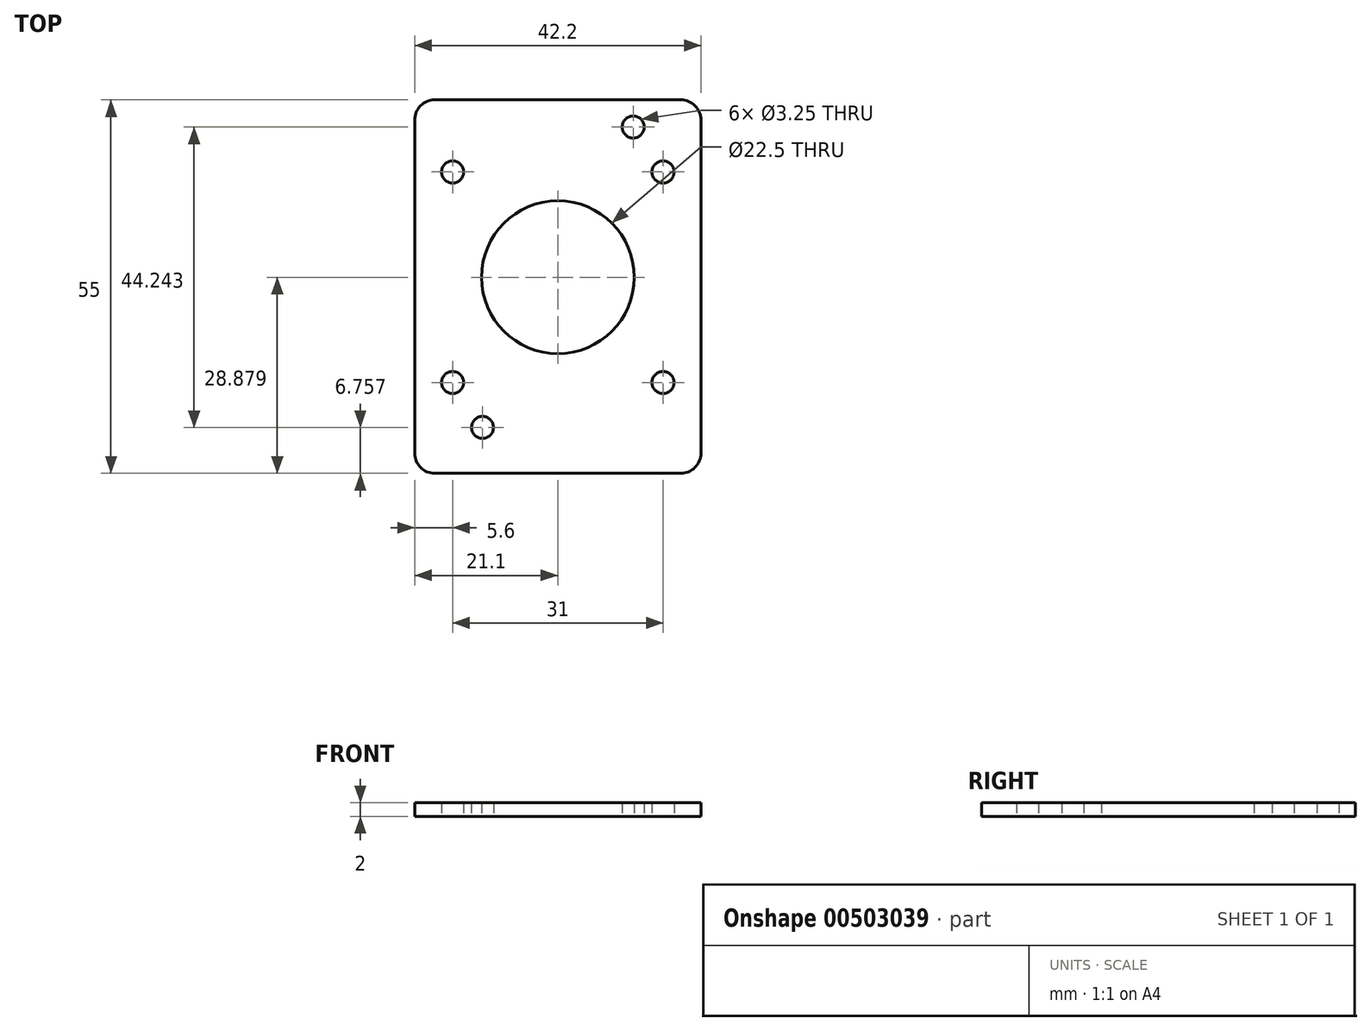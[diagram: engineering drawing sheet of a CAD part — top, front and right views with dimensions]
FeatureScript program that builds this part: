
annotation { "Feature Type Name" : "Feature", "Feature Type Description" : "" }
export const myFeature = defineFeature(function(context is Context, id is Id, definition is map)
    precondition{}
    {
        {
            var Q0;
            Q0=qCreatedBy(makeId("Top.planeOp"),FACE);
            var sketch = newSketch(context, id + "F0", { "sketchPlane" : qUnion([Q0])});
            skLineSegment(sketch, "E0.bottom", {"start": v(0, 0) * mm, "end": v(42.2, 0) * mm});
            skLineSegment(sketch, "E0.top", {"start": v(0, 55) * mm, "end": v(42.2, 55) * mm});
            skLineSegment(sketch, "E0.left", {"start": v(0, 0) * mm, "end": v(0, 55) * mm});
            skLineSegment(sketch, "E0.right", {"start": v(42.2, 0) * mm, "end": v(42.2, 55) * mm});
            skCircle(sketch, "E1", {"center": v(32.2, 51) * mm, "radius": 1.63 * mm});
            skLineSegment(sketch, "E2", {"start": v(32.2, 51) * mm, "end": v(10, 6.76) * mm});
            skCircle(sketch, "E3", {"center": v(21.1, 28.88) * mm, "radius": 11.25 * mm});
            skLineSegment(sketch, "E4", {"start": v(21.1, 55) * mm, "end": v(21.1, 0) * mm, "construction": true});
            skCircle(sketch, "E5", {"center": v(10, 6.76) * mm, "radius": 1.63 * mm});
            skLineSegment(sketch, "E6.bottom", {"start": v(5.6, 44.38) * mm, "end": v(36.6, 44.38) * mm});
            skLineSegment(sketch, "E6.top", {"start": v(5.6, 13.38) * mm, "end": v(36.6, 13.38) * mm});
            skLineSegment(sketch, "E6.left", {"start": v(5.6, 44.38) * mm, "end": v(5.6, 13.38) * mm});
            skLineSegment(sketch, "E6.right", {"start": v(36.6, 44.38) * mm, "end": v(36.6, 13.38) * mm});
            skCircle(sketch, "E7", {"center": v(5.6, 44.38) * mm, "radius": 1.63 * mm});
            skCircle(sketch, "E8", {"center": v(36.6, 44.38) * mm, "radius": 1.63 * mm});
            skCircle(sketch, "E9", {"center": v(36.6, 13.38) * mm, "radius": 1.63 * mm});
            skCircle(sketch, "E10", {"center": v(5.6, 13.38) * mm, "radius": 1.63 * mm});
            skSolve(sketch);
        }
        {
            var Q0;
            Q0=makeQuery(id+"F0.imprint","IMPRINT",FACE,{"disambiguationData":[TD([[makeQuery(id+"F0.imprint","IMPRINT",EDGE,{"derivedFrom":sQuery(id+"F0.wireOp",EDGE,"E0.bottom")}),1.0]])]});
            var Q1;
            {var subQ1=sQuery(id+"F0.wireOp",EDGE,"E2");var subQ4=sQuery(id+"F0.wireOp",EDGE,"E6.bottom");var subQ5=makeQuery(id+"F0.imprint","INTERSECT",VERTEX,{"derivedFrom":[subQ1,subQ4]});Q1=makeQuery(id+"F0.imprint","IMPRINT",FACE,{"disambiguationData":[TD([[makeQuery(id+"F0.imprint","IMPRINT",EDGE,{"disambiguationData":[TD([[subQ5,-1.0]])],"derivedFrom":subQ1}),-1.0]])]});}
            var Q2;
            {var subQ0=sQuery(id+"F0.wireOp",EDGE,"E6.bottom");var subQ1=sQuery(id+"F0.wireOp",EDGE,"E2");var subQ2=makeQuery(id+"F0.imprint","INTERSECT",VERTEX,{"derivedFrom":[subQ1,subQ0]});Q2=makeQuery(id+"F0.imprint","IMPRINT",FACE,{"disambiguationData":[TD([[makeQuery(id+"F0.imprint","IMPRINT",EDGE,{"disambiguationData":[TD([[subQ2,-1.0]])],"derivedFrom":subQ1}),1.0]])]});}
            extrude(context, id + "F1", {"entities" : qUnion([Q0, Q1, Q2]), "depth" : 2 * mm});
        }
        {
            var Q0;
            Q0=makeQuery(id+"F1.opExtrude","SWEPT_EDGE",EDGE,{"disambiguationData":[OSD([sQuery(id+"F0.wireOp",EDGE,"E0.top"),sQuery(id+"F0.wireOp",EDGE,"E0.right")])]});
            var Q1;
            Q1=makeQuery(id+"F1.opExtrude","SWEPT_EDGE",EDGE,{"disambiguationData":[OSD([sQuery(id+"F0.wireOp",EDGE,"E0.top"),sQuery(id+"F0.wireOp",EDGE,"E0.left")])]});
            var Q2;
            Q2=makeQuery(id+"F1.opExtrude","SWEPT_EDGE",EDGE,{"disambiguationData":[OSD([sQuery(id+"F0.wireOp",EDGE,"E0.bottom"),sQuery(id+"F0.wireOp",EDGE,"E0.left")])]});
            var Q3;
            Q3=makeQuery(id+"F1.opExtrude","SWEPT_EDGE",EDGE,{"disambiguationData":[OSD([sQuery(id+"F0.wireOp",EDGE,"E0.bottom"),sQuery(id+"F0.wireOp",EDGE,"E0.right")])]});
            fillet(context, id + "F2", {"entities" : qUnion([Q0, Q1, Q2, Q3]), "radius" : 3 * mm, "tangentPropagation" : true, "allowEdgeOverflow" : false});
        }
    });
